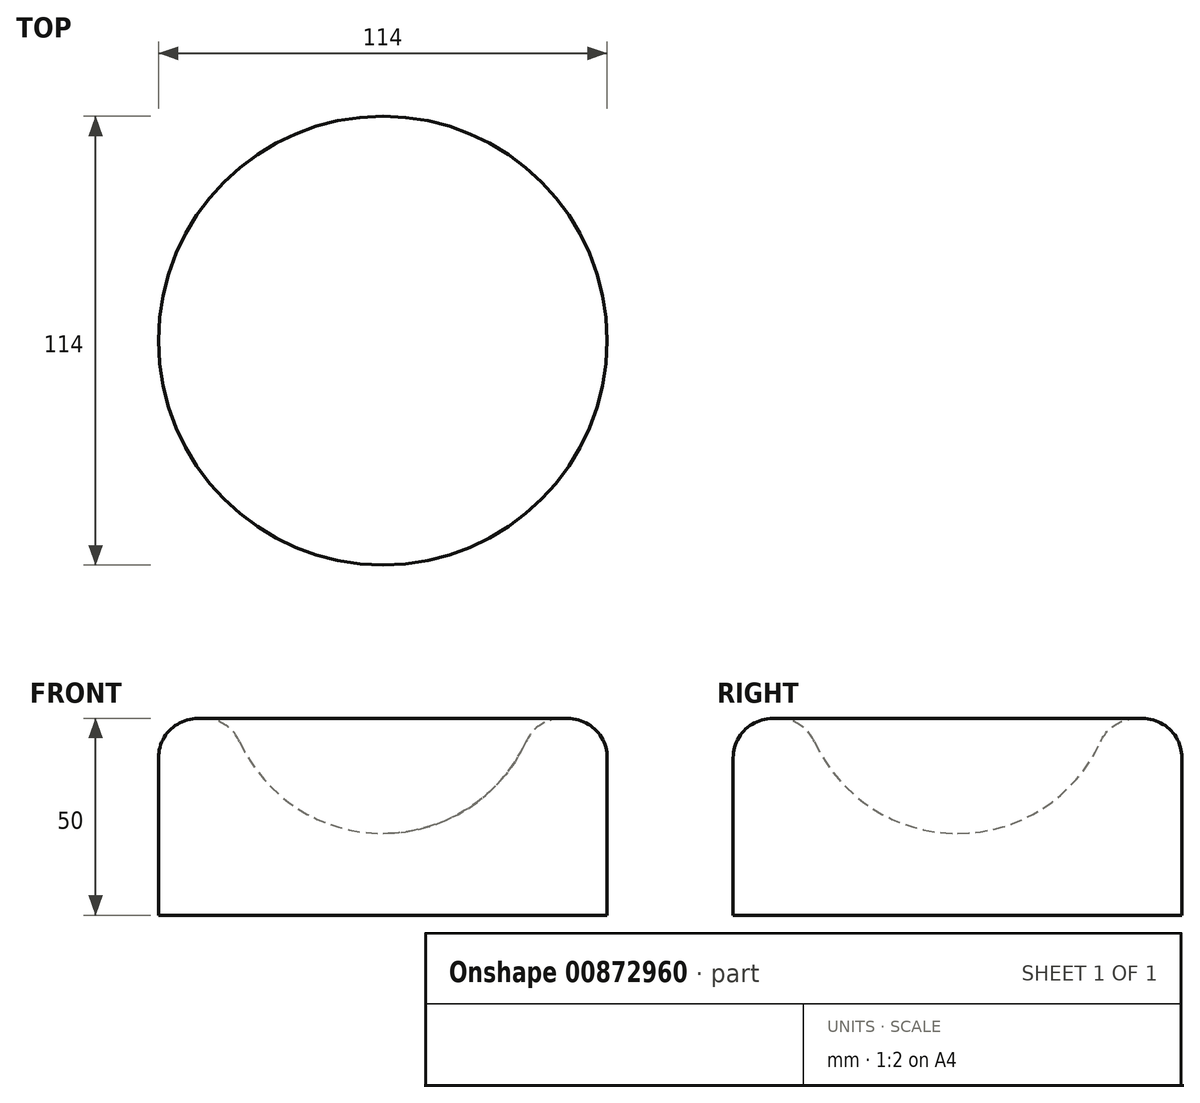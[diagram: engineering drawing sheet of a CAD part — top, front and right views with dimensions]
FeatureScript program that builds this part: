
annotation { "Feature Type Name" : "Feature", "Feature Type Description" : "" }
export const myFeature = defineFeature(function(context is Context, id is Id, definition is map)
    precondition{}
    {
        {
            var Q0;
            Q0=qCreatedBy(makeId("Top.planeOp"),FACE);
            var sketch = newSketch(context, id + "F0", { "sketchPlane" : qUnion([Q0])});
            skPoint(sketch, "E0.middle", {"position": v(0, 0) * mm});
            skCircle(sketch, "E1", {"center": v(0, 0) * mm, "radius": 57 * mm});
            skSolve(sketch);
        }
        {
            var Q0;
            Q0=qCreatedBy(makeId("Front.planeOp"),FACE);
            var sketch = newSketch(context, id + "F1", { "sketchPlane" : qUnion([Q0])});
            skArc(sketch, "E2", {"start": v(0, 20.76) * mm, "mid": v(40, 60.76) * mm, "end": v(0, 100.76) * mm});
            skPoint(sketch, "E2.first.point", {"position": v(-36.8, 45.08) * mm});
            skPoint(sketch, "E2.second.point", {"position": v(36.51, 44.43) * mm});
            skPoint(sketch, "E2.third.point", {"position": v(34.72, 80.63) * mm});
            skLineSegment(sketch, "E3", {"start": v(0, 100.76) * mm, "end": v(0, 20.76) * mm});
            skLineSegment(sketch, "E4", {"start": v(0, 100.76) * mm, "end": v(0, -19.24) * mm, "construction": true});
            skSolve(sketch);
        }
        {
            var Q0;
            Q0=makeQuery(id+"F0.imprint","IMPRINT",FACE,{"disambiguationData":[TD([[makeQuery(id+"F0.imprint","IMPRINT",EDGE,{"derivedFrom":sQuery(id+"F0.wireOp",EDGE,"E1")}),1.0]])]});
            extrude(context, id + "F2", {"entities" : qUnion([Q0]), "depth" : 50 * mm, "offsetDistance" : 25 * mm});
        }
        {
            var Q0;
            Q0=makeQuery(id+"F1.imprint","IMPRINT",FACE,{"disambiguationData":[TD([[makeQuery(id+"F1.imprint","IMPRINT",EDGE,{"derivedFrom":sQuery(id+"F1.wireOp",EDGE,"E2")}),1.0]])]});
            var Q1;
            Q1=sQuery(id+"F1.wireOp",EDGE,"E4");
            revolve(context, id + "F3", {"operationType" : NewBodyOperationType.REMOVE, "surfaceOperationType" : NewSurfaceOperationType.NEW, "entities" : qUnion([Q0]), "axis" : qUnion([Q1]), "revolveType" : RevolveType.FULL, "oppositeDirection" : true});
        }
        {
            var Q0;
            Q0=makeQuery(id+"F2.opExtrude","CAP_FACE",FACE,{"disambiguationData":[OSD([sQuery(id+"F0.wireOp",EDGE,"E1")])],"isStart":false});
            fillet(context, id + "F4", {"entities" : qUnion([Q0]), "radius" : 10 * mm, "allowEdgeOverflow" : false});
        }
    });
